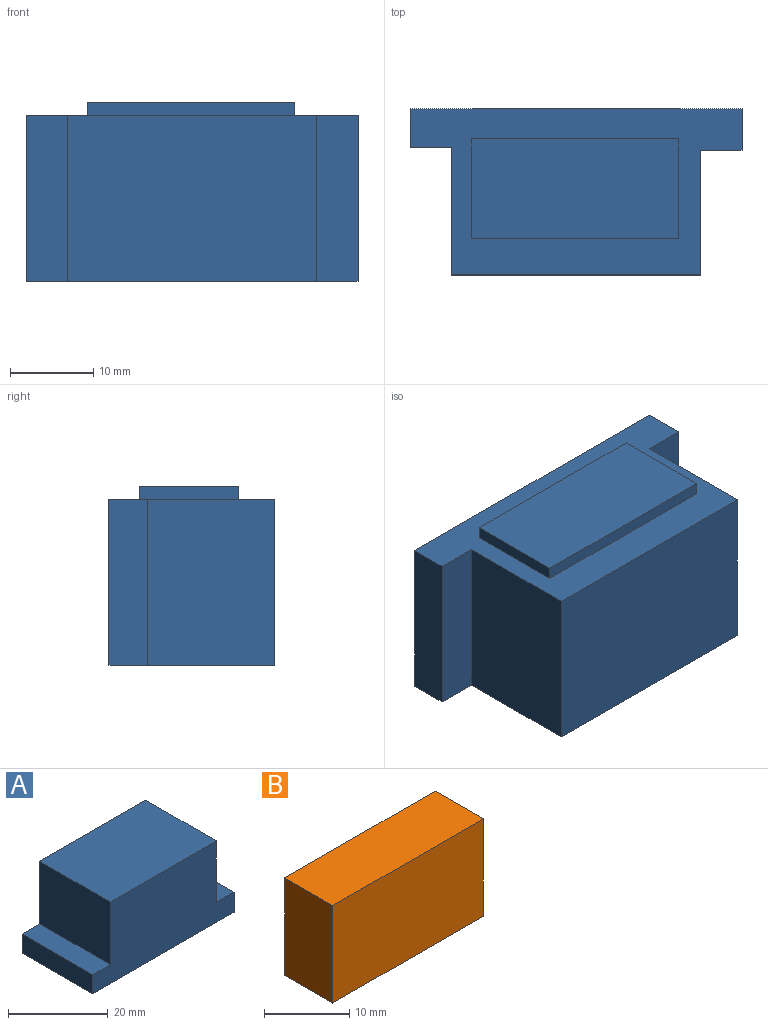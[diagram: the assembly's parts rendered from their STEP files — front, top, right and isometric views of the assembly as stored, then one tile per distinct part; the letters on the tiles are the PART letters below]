
ASSEMBLY  parts=2 mates=2
PART A: 20 faces, bbox 40x21.5x20 mm
  f0: plane 20x15.32mm, normal (-1,0,0), area 306.5mm2, adj f3,f4,f5,f13
  f1: plane 20x15.04mm, normal (1,0,0), area 300.8mm2, adj f3,f4,f5,f11
  f2: plane 40x20mm, normal (0,0,-1), area 425mm2, adj f4,f5,f7,f8,f9,f10,f12,f14
  f3: plane 30x20mm, normal (0,0,1), area 600mm2, adj f0,f1,f4,f5
  f4: plane 40x20mm, normal (0,-1,0), area 648.2mm2, adj f0,f1,f2,f3,f11,f12,f13,f14
  f5: plane 40x20mm, normal (0,1,0), area 348.2mm2, adj f0,f1,f2,f3,f11,f12,f13,f14
  f6: plane 25x15mm, normal (0,0,-1), area 375mm2, adj f7,f8,f9,f10
  f7: plane 17.5x15mm, normal (1,0,0), area 262.5mm2, adj f2,f6,f9,f10
  f8: plane 17.5x15mm, normal (-1,0,0), area 262.5mm2, adj f2,f6,f9,f10
  f9: plane 25x17.5mm, normal (0,1,0), area 437.5mm2, adj f2,f6,f7,f8
  f10: plane 25x17.5mm, normal (0,-1,0), area 437.5mm2, adj f2,f6,f7,f8
  f11: plane 20x5mm, normal (0,0,1), area 100mm2, adj f1,f4,f5,f12
  f12: plane 20x4.96mm, normal (1,0,0), area 99.2mm2, adj f2,f4,f5,f11
  f13: plane 20x5mm, normal (0,0,1), area 100mm2, adj f0,f4,f5,f14
  f14: plane 20x4.68mm, normal (-1,0,0), area 93.5mm2, adj f2,f4,f5,f13
  f15: plane 25x1.5mm, normal (0,0,1), area 37.5mm2, adj f5,f16,f18,f19
  f16: plane 12x1.5mm, normal (1,0,0), area 18mm2, adj f5,f15,f17,f19
  f17: plane 25x1.5mm, normal (0,0,-1), area 37.5mm2, adj f5,f16,f18,f19
  f18: plane 12x1.5mm, normal (-1,0,0), area 18mm2, adj f5,f15,f17,f19
  f19: plane 25x12mm, normal (0,1,0), area 300mm2, adj f15,f16,f17,f18
PART B: 6 faces, bbox 25x8x14 mm
  f0: plane 25x8mm, normal (0,0,1), area 200mm2, adj f1,f3,f4,f5
  f1: plane 14x8mm, normal (-1,0,0), area 112mm2, adj f0,f2,f4,f5
  f2: plane 25x8mm, normal (0,0,-1), area 200mm2, adj f1,f3,f4,f5
  f3: plane 14x8mm, normal (1,0,0), area 112mm2, adj f0,f2,f4,f5
  f4: plane 25x14mm, normal (0,-1,0), area 350mm2, adj f0,f1,f2,f3
  f5: plane 25x14mm, normal (0,1,0), area 350mm2, adj f0,f1,f2,f3
PLACE A rot(axis=(1,0,0),90deg) t=(-35.12,-38.04,25.85)mm
PLACE B t=(-19.57,-85,-36.73)mm
MATE fastened B.f5 <-> B.f2  axis (0,1,0) through (-73.11,-85,15.35)mm
MATE fastened A.f9 <-> B.f2  axis (0,0,1) through (-73.11,-89,8.35)mm
